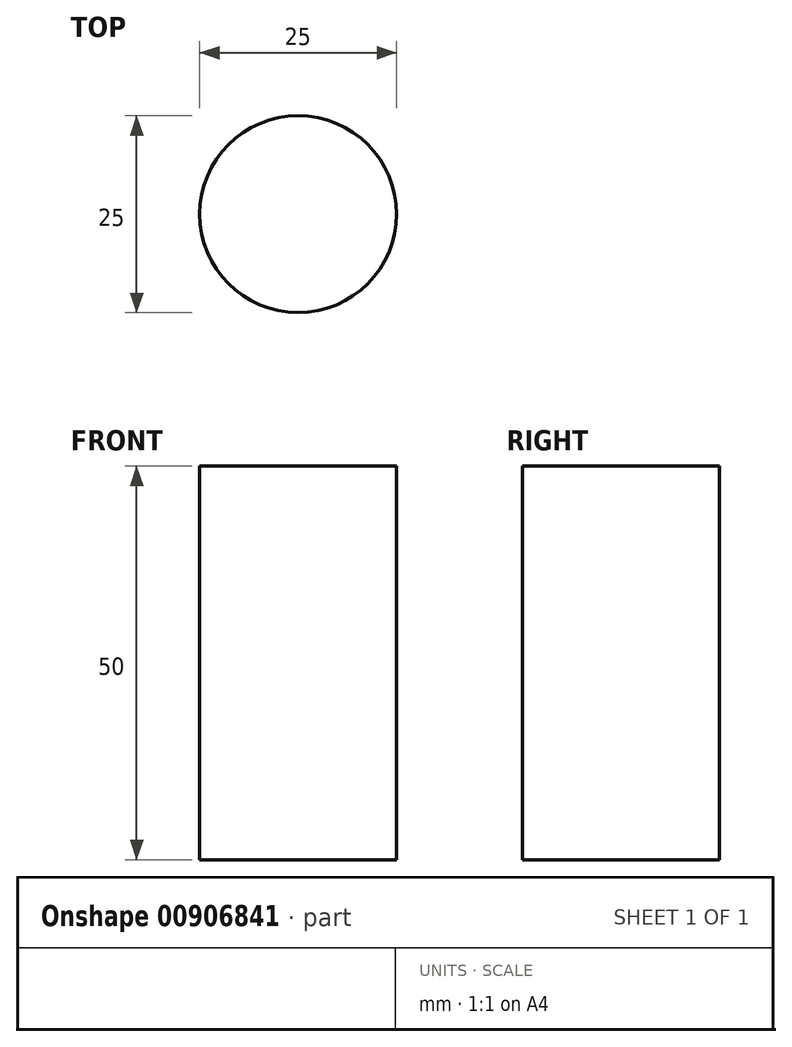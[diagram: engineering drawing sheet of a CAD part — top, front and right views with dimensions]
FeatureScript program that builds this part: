
annotation { "Feature Type Name" : "Feature", "Feature Type Description" : "" }
export const myFeature = defineFeature(function(context is Context, id is Id, definition is map)
    precondition{}
    {
        {
            var Q0;
            Q0=qCreatedBy(makeId("Top.planeOp"),FACE);
            var sketch = newSketch(context, id + "F0", { "sketchPlane" : qUnion([Q0])});
            skCircle(sketch, "E0", {"center": v(0, 0) * mm, "radius": 12.5 * mm});
            skSolve(sketch);
        }
        {
            var Q0;
            Q0=sQuery(id+"F0.wireOp",EDGE,"E0");
            extrude(context, id + "F1", {"bodyType" : ToolBodyType.SURFACE, "surfaceEntities" : qUnion([Q0]), "depth" : 50 * mm, "offsetDistance" : 25 * mm});
        }
    });
